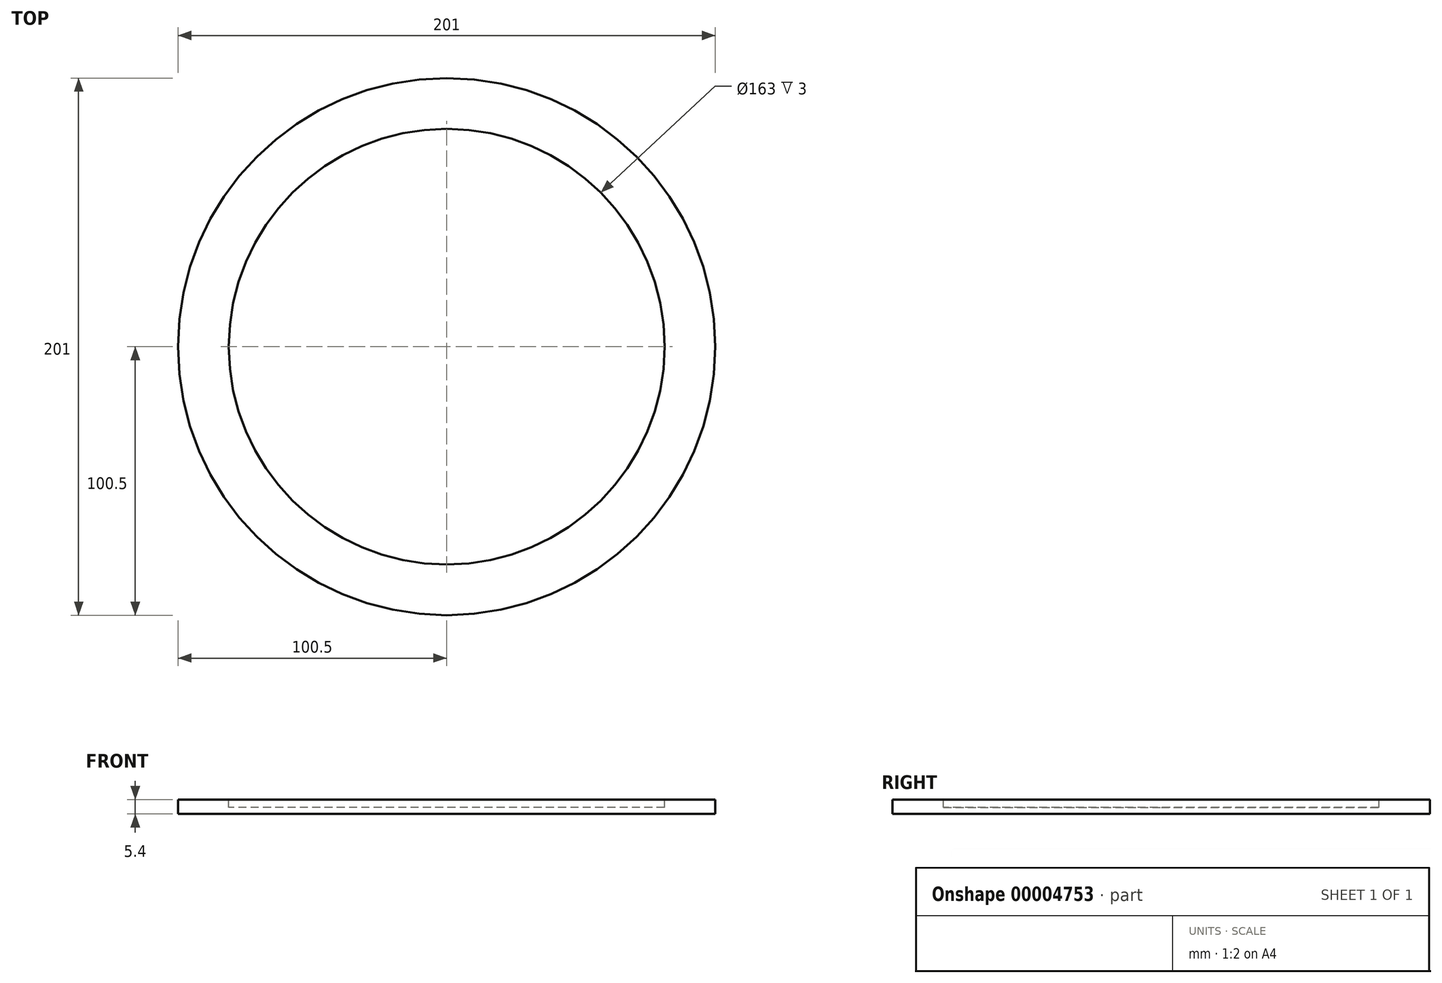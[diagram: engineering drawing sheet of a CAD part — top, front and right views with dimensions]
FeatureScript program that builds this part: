
annotation { "Feature Type Name" : "Feature", "Feature Type Description" : "" }
export const myFeature = defineFeature(function(context is Context, id is Id, definition is map)
    precondition{}
    {
        {
            var Q0;
            Q0=qCreatedBy(makeId("Top.planeOp"),FACE);
            var sketch = newSketch(context, id + "F0", { "sketchPlane" : qUnion([Q0])});
            skCircle(sketch, "E0", {"center": v(0, 0) * mm, "radius": 100.5 * mm});
            skCircle(sketch, "E1", {"center": v(0, 0) * mm, "radius": 81.5 * mm});
            skSolve(sketch);
        }
        {
            var Q0;
            Q0=makeQuery(id+"F0.imprint","IMPRINT",FACE,{"disambiguationData":[TD([[makeQuery(id+"F0.imprint","IMPRINT",EDGE,{"derivedFrom":sQuery(id+"F0.wireOp",EDGE,"E0")}),1.0]])]});
            var Q1;
            Q1=makeQuery(id+"F0.imprint","IMPRINT",FACE,{"disambiguationData":[TD([[makeQuery(id+"F0.imprint","IMPRINT",EDGE,{"derivedFrom":sQuery(id+"F0.wireOp",EDGE,"E1")}),1.0]])]});
            extrude(context, id + "F1", {"entities" : qUnion([Q0, Q1]), "oppositeDirection" : true, "depth" : 5.4 * mm});
        }
        {
            var Q0;
            Q0=makeQuery(id+"F0.imprint","IMPRINT",FACE,{"disambiguationData":[TD([[makeQuery(id+"F0.imprint","IMPRINT",EDGE,{"derivedFrom":sQuery(id+"F0.wireOp",EDGE,"E1")}),1.0]])]});
            extrude(context, id + "F2", {"entities" : qUnion([Q0]), "operationType" : NewBodyOperationType.REMOVE, "oppositeDirection" : true, "depth" : 3 * mm});
        }
    });
